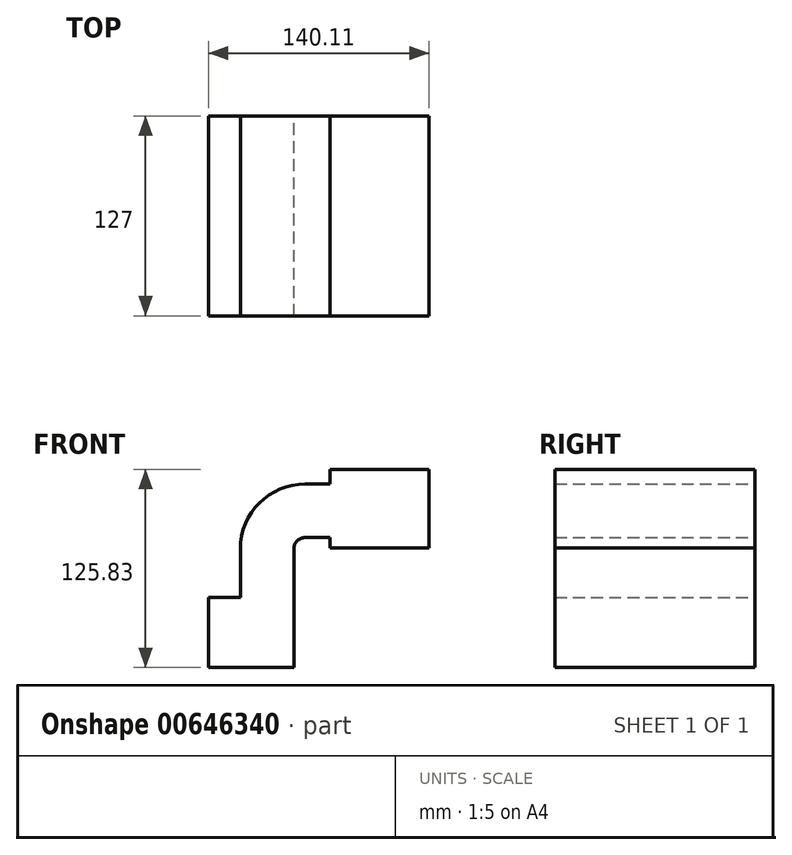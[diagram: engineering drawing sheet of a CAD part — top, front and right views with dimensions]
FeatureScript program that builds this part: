
annotation { "Feature Type Name" : "Feature", "Feature Type Description" : "" }
export const myFeature = defineFeature(function(context is Context, id is Id, definition is map)
    precondition{}
    {
        {
            var Q0;
            Q0=qCreatedBy(makeId("Front.planeOp"),FACE);
            var sketch = newSketch(context, id + "F0", { "sketchPlane" : qUnion([Q0])});
            skLineSegment(sketch, "E0.bottom", {"start": v(27.12, 22.21) * mm, "end": v(-27.12, 22.21) * mm});
            skLineSegment(sketch, "E0.top", {"start": v(27.12, -22.21) * mm, "end": v(-27.12, -22.21) * mm});
            skLineSegment(sketch, "E0.left", {"start": v(27.12, 22.21) * mm, "end": v(27.12, -22.21) * mm});
            skLineSegment(sketch, "E0.right", {"start": v(-27.12, 22.21) * mm, "end": v(-27.12, -22.21) * mm});
            skPoint(sketch, "E0.middle", {"position": v(0, 0) * mm});
            skLineSegment(sketch, "E1.bottom", {"start": v(112.99, 53.84) * mm, "end": v(50.15, 53.84) * mm});
            skLineSegment(sketch, "E1.top", {"start": v(112.99, 103.62) * mm, "end": v(50.15, 103.62) * mm});
            skLineSegment(sketch, "E1.left", {"start": v(112.99, 53.84) * mm, "end": v(112.99, 103.62) * mm});
            skLineSegment(sketch, "E1.right", {"start": v(50.15, 53.84) * mm, "end": v(50.15, 103.62) * mm});
            skPoint(sketch, "E1.middle", {"position": v(81.57, 78.73) * mm});
            skLineSegment(sketch, "E2", {"start": v(27.12, 22.21) * mm, "end": v(27.12, 53.15) * mm});
            skArc(sketch, "E3", {"start": v(27.12, 53.15) * mm, "mid": v(29.24, 58.27) * mm, "end": v(34.36, 60.4) * mm});
            skLineSegment(sketch, "E4", {"start": v(34.36, 60.4) * mm, "end": v(81.8, 60.4) * mm});
            skLineSegment(sketch, "E5.0", {"start": v(34.36, 94.37) * mm, "end": v(81.8, 94.37) * mm});
            skArc(sketch, "E5.1", {"start": v(-6.86, 53.15) * mm, "mid": v(5.21, 82.3) * mm, "end": v(34.36, 94.37) * mm});
            skLineSegment(sketch, "E5.2", {"start": v(-6.86, 22.21) * mm, "end": v(-6.86, 53.15) * mm});
            skSolve(sketch);
        }
        {
            var Q0;
            Q0 = qSketchRegion(id + "F0", true);
            extrude(context, id + "F1", {"entities" : qUnion([Q0]), "endBound" : BoundingType.SYMMETRIC, "depth" : 127 * mm, "offsetDistance" : 25.4 * mm});
        }
    });
